# Revit family: Sink-Wall_Mount-Lavatory-KOHLER-Rêve-K-5150_1
name_source: partatom
category: Plumbing Fixtures
revit_build: Autodesk Revit 2015 (Build: 20140606_1530(x64)
units: mm (PartAtom-declared; Revit-internal decimal feet)

## types (6) — shared parameters
ADA Compliant = No
Assembly Code = D2010400
CW Connection = No
Cold Water Inlet = Cold Water Inlet
Date Modified = 4/8/2019
Default Elevation = 36"
Drain Included = No
HW Connection = No
Height = 17 5/16"
Hot Water Inlet = Hot Water Inlet
Length = 23 5/8"
Manufacturer = KOHLER Co.
MasterFormat 1995 = 15410
MasterFormat 2004 = 22.41.16
Material = Fireclay
Product Documentation Link = https://www.us.kohler.com
Product Name = Reve
Product Page URL = http://www.us.kohler.com
URL = https://www.us.kohler.com
Vent Connection = No
Waste Connection = Yes
Waste Water Outlet = Waste Water Outlet
WaterSense Certified = No
Width = 18 5/16"

## per-type parameters (varying)
| type | 1_Hole | 3_Hole | Description | Finish | Model | Type |
| Single Hole-0-White | Yes | No | 23inch semi-pedestal bathroom sink with single faucet hole and shroud | Kohler-Fireclay-0-White | K-5150-1-0 | 1 |
| Single Hole-96-Biscuit | Yes | No | 23inch semi-pedestal bathroom sink with single faucet hole and shroud | Kohler-Fireclay-96-Biscuit | K-5150-1-96 | 2 |
| Single Hole-47-Almond | Yes | No | 23inch semi-pedestal bathroom sink with single faucet hole and shroud | Kohler-Fireclay-47-Almond | K-5150-1-47 | 3 |
| 8 inch Holes, 0-White | No | Yes | 23inch semi-pedestal bathroom sink with 8inch widespread faucet holes and shroud | Kohler-Fireclay-0-White | K-5150-8-0 | 4 |
| 8 inch Holes, 47-Almond | No | Yes | 23inch semi-pedestal bathroom sink with 8inch widespread faucet holes and shroud | Kohler-Fireclay-47-Almond | K-5150-8-47 | 5 |
| 8 inch Holes, 96-Biscuit | No | Yes | 23inch semi-pedestal bathroom sink with 8inch widespread faucet holes and shroud | Kohler-Fireclay-96-Biscuit | K-5150-8-96 | 6 |

## geometry (parser evidence)
native form markers: Sweep x5
no freeform markers — native parametric forms only
